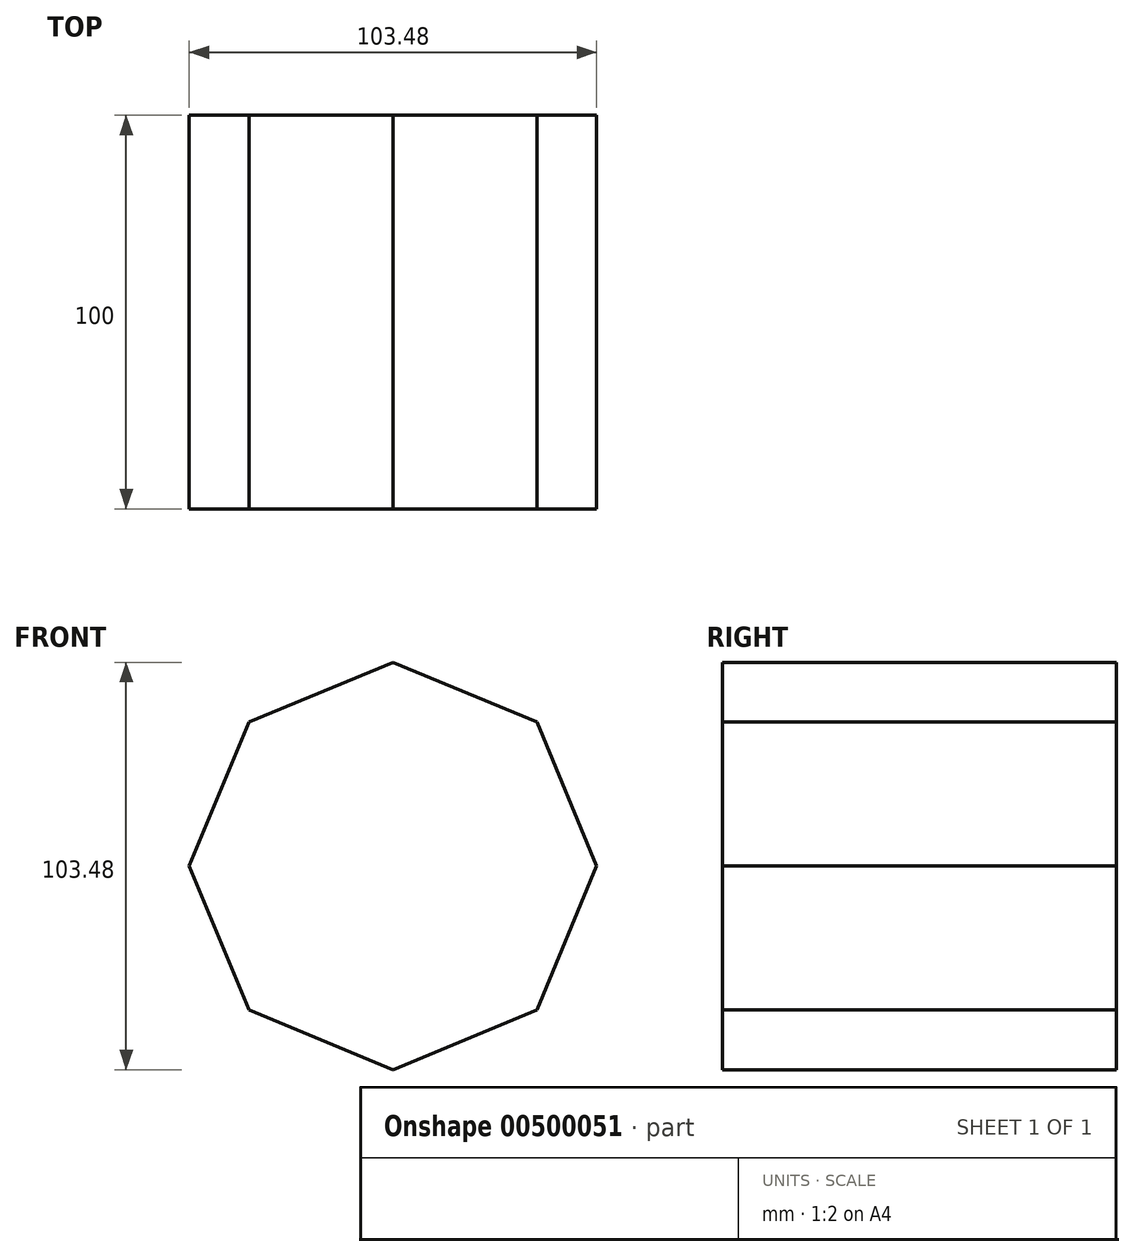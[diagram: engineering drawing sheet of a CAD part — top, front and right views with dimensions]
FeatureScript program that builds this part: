
annotation { "Feature Type Name" : "Feature", "Feature Type Description" : "" }
export const myFeature = defineFeature(function(context is Context, id is Id, definition is map)
    precondition{}
    {
        {
            var Q0;
            Q0=qCreatedBy(makeId("Front.planeOp"),FACE);
            var sketch = newSketch(context, id + "F0", { "sketchPlane" : qUnion([Q0])});
            skCircle(sketch, "E0.cCircle", {"center": v(0, 0) * mm, "radius": 51.74 * mm, "construction": true});
            skLineSegment(sketch, "E0.0", {"start": v(0, 51.74) * mm, "end": v(36.58, 36.58) * mm});
            skLineSegment(sketch, "E0.1", {"start": v(36.58, 36.58) * mm, "end": v(51.74, 0) * mm});
            skLineSegment(sketch, "E0.2", {"start": v(51.74, 0) * mm, "end": v(36.58, -36.58) * mm});
            skLineSegment(sketch, "E0.3", {"start": v(36.58, -36.58) * mm, "end": v(0, -51.74) * mm});
            skLineSegment(sketch, "E0.4", {"start": v(0, -51.74) * mm, "end": v(-36.58, -36.58) * mm});
            skLineSegment(sketch, "E0.5", {"start": v(-36.58, -36.58) * mm, "end": v(-51.74, 0) * mm});
            skLineSegment(sketch, "E0.6", {"start": v(-51.74, 0) * mm, "end": v(-36.58, 36.58) * mm});
            skLineSegment(sketch, "E0.7", {"start": v(-36.58, 36.58) * mm, "end": v(0, 51.74) * mm});
            skSolve(sketch);
        }
        {
            var Q0;
            Q0 = qSketchRegion(id + "F0", true);
            extrude(context, id + "F1", {"entities" : qUnion([Q0]), "endBound" : BoundingType.SYMMETRIC, "depth" : 100 * mm});
        }
    });
